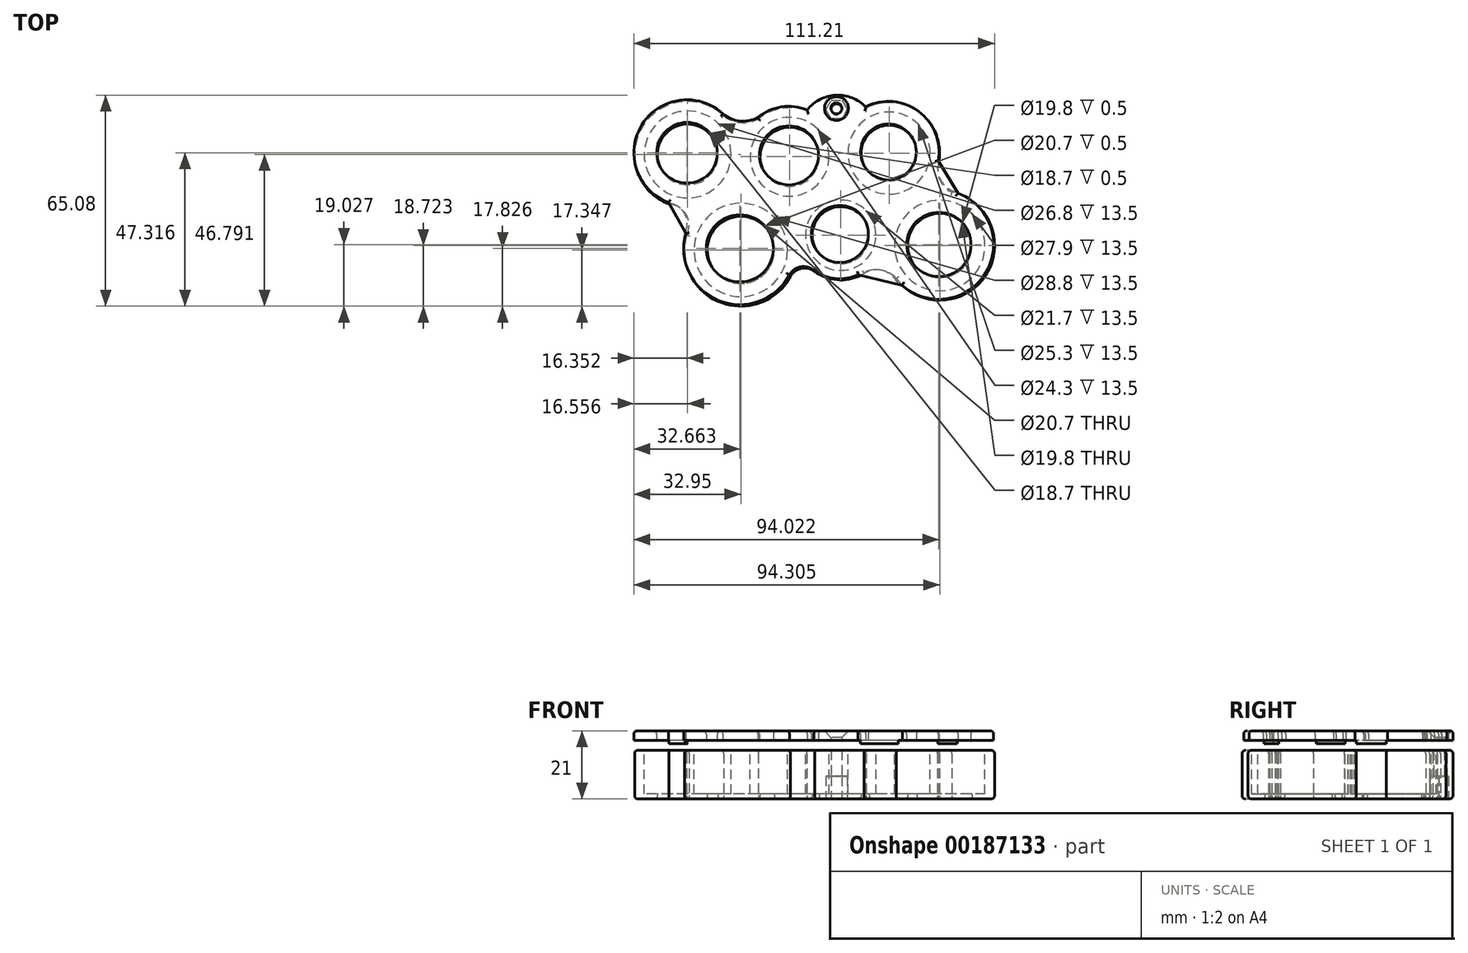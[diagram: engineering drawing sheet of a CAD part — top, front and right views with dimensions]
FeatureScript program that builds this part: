
annotation { "Feature Type Name" : "Feature", "Feature Type Description" : "" }
export const myFeature = defineFeature(function(context is Context, id is Id, definition is map)
    precondition{}
    {
        {
            var Q0;
            Q0=qCreatedBy(makeId("Top.planeOp"),FACE);
            var sketch = newSketch(context, id + "F0", { "sketchPlane" : qUnion([Q0])});
            skArc(sketch, "E0", {"start": v(-18.22, 23.12) * mm, "mid": v(-43.25, 19.71) * mm, "end": v(-35.08, -4.19) * mm});
            skArc(sketch, "E1", {"start": v(7.41, 24.56) * mm, "mid": v(-0.37, 25.32) * mm, "end": v(-7.48, 22.09) * mm});
            skArc(sketch, "E2", {"start": v(48.15, 8.81) * mm, "mid": v(42.1, 24.06) * mm, "end": v(25.77, 25.48) * mm});
            skArc(sketch, "E3", {"start": v(9.86, -25.02) * mm, "mid": v(17.41, -27.58) * mm, "end": v(25.12, -25.54) * mm});
            skArc(sketch, "E4", {"start": v(34.96, -27.17) * mm, "mid": v(62.62, -26.1) * mm, "end": v(52.17, -0.47) * mm});
            skArc(sketch, "E5", {"start": v(-29.65, -13.66) * mm, "mid": v(-19.4, -34.43) * mm, "end": v(2.37, -26.49) * mm});
            skArc(sketch, "E6", {"start": v(-29.65, -13.66) * mm, "mid": v(-29.77, -7.44) * mm, "end": v(-35.08, -4.19) * mm});
            skArc(sketch, "E7", {"start": v(-18.22, 23.12) * mm, "mid": v(-13.01, 20.97) * mm, "end": v(-7.48, 22.09) * mm});
            skArc(sketch, "E8", {"start": v(48.15, 8.81) * mm, "mid": v(48.38, 3.4) * mm, "end": v(52.17, -0.47) * mm});
            skArc(sketch, "E9", {"start": v(34.96, -27.17) * mm, "mid": v(30.34, -24.58) * mm, "end": v(25.12, -25.54) * mm});
            skArc(sketch, "E10", {"start": v(9.86, -25.02) * mm, "mid": v(5.77, -24) * mm, "end": v(2.37, -26.49) * mm});
            skCircle(sketch, "E11", {"center": v(-29.33, 11.12) * mm, "radius": 9.35 * mm});
            skCircle(sketch, "E12", {"center": v(-12.94, -18.32) * mm, "radius": 10.35 * mm});
            skCircle(sketch, "E13", {"center": v(2.1, 10.43) * mm, "radius": 9.1 * mm});
            skCircle(sketch, "E14", {"center": v(17.88, -13.8) * mm, "radius": 8.8 * mm});
            skCircle(sketch, "E15", {"center": v(32.79, 11.55) * mm, "radius": 8.6 * mm});
            skCircle(sketch, "E16", {"center": v(48.42, -16.95) * mm, "radius": 9.9 * mm});
            skPoint(sketch, "E17", {"position": v(17.46, 2.98) * mm});
            skPoint(sketch, "E18.orphan", {"position": v(17.45, 10.99) * mm});
            skPoint(sketch, "E19.orphan", {"position": v(25.33, -1.12) * mm});
            skPoint(sketch, "E20.trimOffspring.end.orphan", {"position": v(10, -1.68) * mm});
            skPoint(sketch, "E21.center.orphan", {"position": v(16.6, 25.02) * mm});
            skArc(sketch, "E22", {"start": v(25.77, 25.48) * mm, "mid": v(16.38, 29.3) * mm, "end": v(7.41, 24.56) * mm});
            skCircle(sketch, "E23", {"center": v(16.6, 25.02) * mm, "radius": 1.7 * mm});
            skSolve(sketch);
        }
        {
            var Q0;
            Q0=makeQuery(id+"F0.imprint","IMPRINT",FACE,{"disambiguationData":[TD([[makeQuery(id+"F0.imprint","IMPRINT",EDGE,{"derivedFrom":sQuery(id+"F0.wireOp",EDGE,"E0")}),1.0]])]});
            extrude(context, id + "F1", {"entities" : qUnion([Q0]), "depth" : 15 * mm});
        }
        {
            var Q0;
            Q0=qCreatedBy(makeId("Top.planeOp"),FACE);
            cPlane(context, id + "F2", {"entities" : qUnion([Q0]), "cplaneType" : CPlaneType.OFFSET, "offset" : 18 * mm, "width" : 150 * mm, "height" : 150 * mm});
        }
        {
            var Q0;
            Q0=makeQuery(id+"F1.opExtrude","CAP_FACE",FACE,{"disambiguationData":[OSD([sQuery(id+"F0.wireOp",EDGE,"E0"),sQuery(id+"F0.wireOp",EDGE,"E1"),sQuery(id+"F0.wireOp",EDGE,"E2"),sQuery(id+"F0.wireOp",EDGE,"E3"),sQuery(id+"F0.wireOp",EDGE,"E4"),sQuery(id+"F0.wireOp",EDGE,"E5"),sQuery(id+"F0.wireOp",EDGE,"E6"),sQuery(id+"F0.wireOp",EDGE,"E7"),sQuery(id+"F0.wireOp",EDGE,"E8"),sQuery(id+"F0.wireOp",EDGE,"E9"),sQuery(id+"F0.wireOp",EDGE,"E10"),sQuery(id+"F0.wireOp",EDGE,"cmuSQvfR-1LlV-bjM8-RssA-lsbDypLqzE8I"),sQuery(id+"F0.wireOp",EDGE,"E21"),sQuery(id+"F0.wireOp",EDGE,"E11"),sQuery(id+"F0.wireOp",EDGE,"E12"),sQuery(id+"F0.wireOp",EDGE,"E13"),sQuery(id+"F0.wireOp",EDGE,"E14"),sQuery(id+"F0.wireOp",EDGE,"E15"),sQuery(id+"F0.wireOp",EDGE,"E16")])],"isStart":false});
            var sketch = newSketch(context, id + "F3", { "sketchPlane" : qUnion([Q0])});
            skCircle(sketch, "E24", {"center": v(-29.33, 11.12) * mm, "radius": 13.4 * mm});
            skCircle(sketch, "E25", {"center": v(-12.94, -18.32) * mm, "radius": 14.4 * mm});
            skCircle(sketch, "E26", {"center": v(17.88, -13.8) * mm, "radius": 10.85 * mm});
            skCircle(sketch, "E27", {"center": v(2.1, 10.43) * mm, "radius": 12.15 * mm});
            skCircle(sketch, "E28", {"center": v(32.79, 11.55) * mm, "radius": 12.65 * mm});
            skCircle(sketch, "E29", {"center": v(48.42, -16.95) * mm, "radius": 13.95 * mm});
            skSolve(sketch);
        }
        {
            var Q0;
            Q0=makeQuery(id+"F3.imprint","IMPRINT",FACE,{"disambiguationData":[TD([[makeQuery(id+"F3.imprint","IMPRINT",EDGE,{"derivedFrom":sQuery(id+"F3.wireOp",EDGE,"E24")}),1.0]])]});
            var Q1;
            Q1=makeQuery(id+"F3.imprint","IMPRINT",FACE,{"disambiguationData":[TD([[makeQuery(id+"F3.imprint","IMPRINT",EDGE,{"derivedFrom":sQuery(id+"F3.wireOp",EDGE,"E27")}),1.0]])]});
            var Q2;
            Q2=makeQuery(id+"F3.imprint","IMPRINT",FACE,{"disambiguationData":[TD([[makeQuery(id+"F3.imprint","IMPRINT",EDGE,{"derivedFrom":sQuery(id+"F3.wireOp",EDGE,"E28")}),1.0]])]});
            var Q3;
            Q3=makeQuery(id+"F3.imprint","IMPRINT",FACE,{"disambiguationData":[TD([[makeQuery(id+"F3.imprint","IMPRINT",EDGE,{"derivedFrom":sQuery(id+"F3.wireOp",EDGE,"E26")}),1.0]])]});
            var Q4;
            Q4=makeQuery(id+"F3.imprint","IMPRINT",FACE,{"disambiguationData":[TD([[makeQuery(id+"F3.imprint","IMPRINT",EDGE,{"derivedFrom":sQuery(id+"F3.wireOp",EDGE,"E25")}),1.0]])]});
            var Q5;
            Q5=makeQuery(id+"F3.imprint","IMPRINT",FACE,{"disambiguationData":[TD([[makeQuery(id+"F3.imprint","IMPRINT",EDGE,{"derivedFrom":sQuery(id+"F3.wireOp",EDGE,"E29")}),1.0]])]});
            extrude(context, id + "F4", {"entities" : qUnion([Q0, Q1, Q2, Q3, Q4, Q5]), "operationType" : NewBodyOperationType.REMOVE, "oppositeDirection" : true, "depth" : 13.5 * mm});
        }
        {
            var Q0;
            Q0=qCreatedBy(makeId("Top.planeOp"),FACE);
            var sketch = newSketch(context, id + "F5", { "sketchPlane" : qUnion([Q0])});
            skPoint(sketch, "E30", {"position": v(16.6, 25.02) * mm});
            skCircle(sketch, "E31.cCircle", {"center": v(16.6, 25.02) * mm, "radius": 2.86 * mm, "construction": true});
            skLineSegment(sketch, "E31.0", {"start": v(18.2, 27.9) * mm, "end": v(19.9, 25.08) * mm});
            skLineSegment(sketch, "E31.1", {"start": v(19.9, 25.08) * mm, "end": v(18.29, 22.2) * mm});
            skLineSegment(sketch, "E31.2", {"start": v(18.29, 22.2) * mm, "end": v(14.99, 22.14) * mm});
            skLineSegment(sketch, "E31.3", {"start": v(14.99, 22.14) * mm, "end": v(13.3, 24.97) * mm});
            skLineSegment(sketch, "E31.4", {"start": v(13.3, 24.97) * mm, "end": v(14.9, 27.85) * mm});
            skLineSegment(sketch, "E31.5", {"start": v(14.9, 27.85) * mm, "end": v(18.2, 27.9) * mm});
            skPoint(sketch, "E31.0.midPoint", {"position": v(19.04, 26.5) * mm});
            skSolve(sketch);
        }
        {
            var Q0;
            Q0=makeQuery(id+"F5.imprint","IMPRINT",FACE,{"disambiguationData":[TD([[makeQuery(id+"F5.imprint","IMPRINT",EDGE,{"derivedFrom":sQuery(id+"F5.wireOp",EDGE,"E31.0")}),-1.0]])]});
            extrude(context, id + "F6", {"entities" : qUnion([Q0]), "operationType" : NewBodyOperationType.REMOVE, "depth" : 7 * mm});
        }
        {
            var Q0;
            Q0=qCreatedBy(id+"F2.planeOp",FACE);
            var sketch = newSketch(context, id + "F7", { "sketchPlane" : qUnion([Q0])});
            skArc(sketch, "E32", {"start": v(-18.43, 23.64) * mm, "mid": v(-43.45, 20.24) * mm, "end": v(-35.28, -3.66) * mm});
            skArc(sketch, "E33", {"start": v(7.53, 24.87) * mm, "mid": v(-0.4, 25.79) * mm, "end": v(-7.7, 22.52) * mm});
            skArc(sketch, "E34", {"start": v(47.94, 9.16) * mm, "mid": v(41.9, 24.4) * mm, "end": v(25.57, 25.83) * mm});
            skArc(sketch, "E35", {"start": v(9.59, -24.63) * mm, "mid": v(17.14, -27.2) * mm, "end": v(24.85, -25.15) * mm});
            skArc(sketch, "E36", {"start": v(34.68, -26.87) * mm, "mid": v(62.34, -25.8) * mm, "end": v(51.88, -0.16) * mm});
            skArc(sketch, "E37", {"start": v(-29.94, -13.18) * mm, "mid": v(-19.68, -33.95) * mm, "end": v(2.08, -26) * mm});
            skArc(sketch, "E38", {"start": v(-29.94, -13.18) * mm, "mid": v(-30, -6.96) * mm, "end": v(-35.28, -3.66) * mm});
            skArc(sketch, "E39", {"start": v(-18.43, 23.64) * mm, "mid": v(-13.23, 21.45) * mm, "end": v(-7.7, 22.52) * mm});
            skArc(sketch, "E40", {"start": v(47.94, 9.16) * mm, "mid": v(48.13, 3.75) * mm, "end": v(51.88, -0.16) * mm});
            skArc(sketch, "E41", {"start": v(34.68, -26.87) * mm, "mid": v(30.07, -24.23) * mm, "end": v(24.85, -25.15) * mm});
            skArc(sketch, "E42", {"start": v(9.59, -24.63) * mm, "mid": v(5.51, -23.57) * mm, "end": v(2.08, -26) * mm});
            skCircle(sketch, "E43", {"center": v(-29.54, 11.65) * mm, "radius": 9.35 * mm});
            skCircle(sketch, "E44", {"center": v(-13.23, -17.84) * mm, "radius": 10.35 * mm});
            skCircle(sketch, "E45", {"center": v(1.9, 10.86) * mm, "radius": 9.1 * mm});
            skCircle(sketch, "E46", {"center": v(17.6, -13.4) * mm, "radius": 8.8 * mm});
            skCircle(sketch, "E47", {"center": v(32.59, 11.9) * mm, "radius": 8.6 * mm});
            skCircle(sketch, "E48", {"center": v(48.13, -16.64) * mm, "radius": 9.9 * mm});
            skLineSegment(sketch, "E49", {"start": v(-29.94, -13.18) * mm, "end": v(-35.28, -3.66) * mm});
            skArc(sketch, "E50", {"start": v(-30.11, -12.87) * mm, "mid": v(-30.27, -7.1) * mm, "end": v(-35.1, -3.97) * mm});
            skArc(sketch, "E51", {"start": v(34.2, -26.79) * mm, "mid": v(30.02, -24.52) * mm, "end": v(25.32, -25.23) * mm});
            skLineSegment(sketch, "E52", {"start": v(54.05, -0.81) * mm, "end": v(47.94, 9.16) * mm});
            skArc(sketch, "E53", {"start": v(48.15, 8.83) * mm, "mid": v(48.9, 2.9) * mm, "end": v(53.84, -0.48) * mm});
            skArc(sketch, "E54", {"start": v(35.61, -28.94) * mm, "mid": v(30.44, -24.61) * mm, "end": v(23.89, -26.18) * mm});
            skLineSegment(sketch, "E55", {"start": v(23.2, -26.02) * mm, "end": v(36.86, -29.23) * mm});
            skPoint(sketch, "E56.center.orphan", {"position": v(16.55, 25.35) * mm});
            skArc(sketch, "E57", {"start": v(7.53, 24.87) * mm, "mid": v(16.65, 23.42) * mm, "end": v(25.57, 25.83) * mm});
            skArc(sketch, "E58", {"start": v(25.57, 25.83) * mm, "mid": v(16.34, 29.4) * mm, "end": v(7.53, 24.87) * mm});
            skCircle(sketch, "E59", {"center": v(16.55, 25.35) * mm, "radius": 1.7 * mm});
            skSolve(sketch);
        }
        {
            var Q0;
            Q0=qSketchRegion(id+"F7",true);
            extrude(context, id + "F8", {"entities" : qUnion([Q0]), "depth" : 3 * mm});
        }
        {
            var Q0;
            {var subQ0=sQuery(id+"F7.wireOp",EDGE,"abFJn2rG-QnjB-3oZD-kfx5-oWbmogYZg01U");Q0=makeQuery(id+"F7.imprint","IMPRINT",FACE,{"disambiguationData":[TD([[makeQuery(id+"F7.imprint","IMPRINT",EDGE,{"derivedFrom":subQ0}),1.0]])]});}
            var Q1;
            {var subQ0=sQuery(id+"F7.wireOp",EDGE,"E50");Q1=makeQuery(id+"F7.imprint","IMPRINT",FACE,{"disambiguationData":[TD([[makeQuery(id+"F7.imprint","IMPRINT",EDGE,{"derivedFrom":subQ0}),1.0]])]});}
            var Q2;
            {var subQ0=sQuery(id+"F7.wireOp",EDGE,"E51");Q2=makeQuery(id+"F7.imprint","IMPRINT",FACE,{"disambiguationData":[TD([[makeQuery(id+"F7.imprint","IMPRINT",EDGE,{"derivedFrom":subQ0}),1.0]])]});}
            var Q3;
            {var subQ0=sQuery(id+"F7.wireOp",EDGE,"E53");Q3=makeQuery(id+"F7.imprint","IMPRINT",FACE,{"disambiguationData":[TD([[makeQuery(id+"F7.imprint","IMPRINT",EDGE,{"derivedFrom":subQ0}),1.0]])]});}
            var Q4;
            {var subQ1=sQuery(id+"F7.wireOp",EDGE,"E54");var subQ3=makeQuery(id+"F7.imprint","IMPRINT",VERTEX,{"disambiguationData":[OD(0.0)],"derivedFrom":subQ1});Q4=makeQuery(id+"F7.imprint","IMPRINT",FACE,{"disambiguationData":[TD([[makeQuery(id+"F7.imprint","IMPRINT",EDGE,{"disambiguationData":[TD([[subQ3,-1.0]])],"derivedFrom":subQ1}),1.0]])]});}
            extrude(context, id + "F9", {"entities" : qUnion([Q0, Q1, Q2, Q3, Q4]), "operationType" : NewBodyOperationType.ADD, "oppositeDirection" : true, "depth" : 1 * mm});
        }
        {
            var Q0;
            Q0=makeQuery(id+"F1.opExtrude","CAP_EDGE",EDGE,{"disambiguationData":[OSD([sQuery(id+"F0.wireOp",EDGE,"E2")])],"isStart":true});
            var Q1;
            Q1=makeQuery(id+"F1.opExtrude","CAP_EDGE",EDGE,{"disambiguationData":[OSD([sQuery(id+"F0.wireOp",EDGE,"cmuSQvfR-1LlV-bjM8-RssA-lsbDypLqzE8I")])],"isStart":true});
            var Q2;
            Q2=makeQuery(id+"F1.opExtrude","CAP_EDGE",EDGE,{"disambiguationData":[OSD([sQuery(id+"F0.wireOp",EDGE,"E1")])],"isStart":true});
            var Q3;
            Q3=makeQuery(id+"F1.opExtrude","CAP_EDGE",EDGE,{"disambiguationData":[OSD([sQuery(id+"F0.wireOp",EDGE,"E7")])],"isStart":true});
            var Q4;
            Q4=makeQuery(id+"F1.opExtrude","CAP_EDGE",EDGE,{"disambiguationData":[OSD([sQuery(id+"F0.wireOp",EDGE,"E0")])],"isStart":true});
            var Q5;
            Q5=makeQuery(id+"F1.opExtrude","CAP_EDGE",EDGE,{"disambiguationData":[OSD([sQuery(id+"F0.wireOp",EDGE,"E6")])],"isStart":true});
            var Q6;
            Q6=makeQuery(id+"F1.opExtrude","CAP_EDGE",EDGE,{"disambiguationData":[OSD([sQuery(id+"F0.wireOp",EDGE,"E5")])],"isStart":true});
            var Q7;
            Q7=makeQuery(id+"F1.opExtrude","CAP_EDGE",EDGE,{"disambiguationData":[OSD([sQuery(id+"F0.wireOp",EDGE,"E10")])],"isStart":true});
            var Q8;
            Q8=makeQuery(id+"F1.opExtrude","CAP_EDGE",EDGE,{"disambiguationData":[OSD([sQuery(id+"F0.wireOp",EDGE,"E3")])],"isStart":true});
            var Q9;
            Q9=makeQuery(id+"F1.opExtrude","CAP_EDGE",EDGE,{"disambiguationData":[OSD([sQuery(id+"F0.wireOp",EDGE,"E9")])],"isStart":true});
            var Q10;
            Q10=makeQuery(id+"F1.opExtrude","CAP_EDGE",EDGE,{"disambiguationData":[OSD([sQuery(id+"F0.wireOp",EDGE,"E4")])],"isStart":true});
            var Q11;
            Q11=makeQuery(id+"F1.opExtrude","CAP_EDGE",EDGE,{"disambiguationData":[OSD([sQuery(id+"F0.wireOp",EDGE,"E8")])],"isStart":true});
            var Q12;
            Q12=makeQuery(id+"F1.opExtrude","CAP_EDGE",EDGE,{"disambiguationData":[OSD([sQuery(id+"F0.wireOp",EDGE,"E2")])],"isStart":false});
            var Q13;
            Q13=makeQuery(id+"F1.opExtrude","CAP_EDGE",EDGE,{"disambiguationData":[OSD([sQuery(id+"F0.wireOp",EDGE,"cmuSQvfR-1LlV-bjM8-RssA-lsbDypLqzE8I")])],"isStart":false});
            var Q14;
            Q14=makeQuery(id+"F1.opExtrude","CAP_EDGE",EDGE,{"disambiguationData":[OSD([sQuery(id+"F0.wireOp",EDGE,"E1")])],"isStart":false});
            var Q15;
            Q15=makeQuery(id+"F1.opExtrude","CAP_EDGE",EDGE,{"disambiguationData":[OSD([sQuery(id+"F0.wireOp",EDGE,"E7")])],"isStart":false});
            var Q16;
            Q16=makeQuery(id+"F1.opExtrude","CAP_EDGE",EDGE,{"disambiguationData":[OSD([sQuery(id+"F0.wireOp",EDGE,"E0")])],"isStart":false});
            var Q17;
            Q17=makeQuery(id+"F1.opExtrude","CAP_EDGE",EDGE,{"disambiguationData":[OSD([sQuery(id+"F0.wireOp",EDGE,"E6")])],"isStart":false});
            var Q18;
            Q18=makeQuery(id+"F1.opExtrude","CAP_EDGE",EDGE,{"disambiguationData":[OSD([sQuery(id+"F0.wireOp",EDGE,"E5")])],"isStart":false});
            var Q19;
            Q19=makeQuery(id+"F1.opExtrude","CAP_EDGE",EDGE,{"disambiguationData":[OSD([sQuery(id+"F0.wireOp",EDGE,"E10")])],"isStart":false});
            var Q20;
            Q20=makeQuery(id+"F1.opExtrude","CAP_EDGE",EDGE,{"disambiguationData":[OSD([sQuery(id+"F0.wireOp",EDGE,"E3")])],"isStart":false});
            var Q21;
            Q21=makeQuery(id+"F1.opExtrude","CAP_EDGE",EDGE,{"disambiguationData":[OSD([sQuery(id+"F0.wireOp",EDGE,"E9")])],"isStart":false});
            var Q22;
            Q22=makeQuery(id+"F1.opExtrude","CAP_EDGE",EDGE,{"disambiguationData":[OSD([sQuery(id+"F0.wireOp",EDGE,"E4")])],"isStart":false});
            var Q23;
            Q23=makeQuery(id+"F1.opExtrude","CAP_EDGE",EDGE,{"disambiguationData":[OSD([sQuery(id+"F0.wireOp",EDGE,"E8")])],"isStart":false});
            var Q24;
            Q24=makeQuery(id+"F1.opExtrude","CAP_EDGE",EDGE,{"disambiguationData":[OSD([sQuery(id+"F0.wireOp",EDGE,"RsfDVoeq-88MK-O4fM-M0ip-vEhRewOvGteJ")])],"isStart":true});
            var Q25;
            Q25=makeQuery(id+"F1.opExtrude","CAP_EDGE",EDGE,{"disambiguationData":[OSD([sQuery(id+"F0.wireOp",EDGE,"RsfDVoeq-88MK-O4fM-M0ip-vEhRewOvGteJ")])],"isStart":false});
            var Q26;
            Q26=makeQuery(id+"F1.opExtrude","CAP_EDGE",EDGE,{"disambiguationData":[OSD([sQuery(id+"F0.wireOp",EDGE,"E22")])],"isStart":false});
            var Q27;
            Q27=makeQuery(id+"F1.opExtrude","CAP_EDGE",EDGE,{"disambiguationData":[OSD([sQuery(id+"F0.wireOp",EDGE,"E22")])],"isStart":true});
            var Q28;
            Q28=makeQuery(id+"F1.opExtrude","CAP_EDGE",EDGE,{"disambiguationData":[OSD([sQuery(id+"F0.wireOp",EDGE,"E13")])],"isStart":true});
            var Q29;
            Q29=makeQuery(id+"F1.opExtrude","CAP_EDGE",EDGE,{"disambiguationData":[OSD([sQuery(id+"F0.wireOp",EDGE,"E15")])],"isStart":true});
            var Q30;
            Q30=makeQuery(id+"F1.opExtrude","CAP_EDGE",EDGE,{"disambiguationData":[OSD([sQuery(id+"F0.wireOp",EDGE,"E16")])],"isStart":true});
            var Q31;
            Q31=makeQuery(id+"F1.opExtrude","CAP_EDGE",EDGE,{"disambiguationData":[OSD([sQuery(id+"F0.wireOp",EDGE,"E14")])],"isStart":true});
            var Q32;
            Q32=makeQuery(id+"F1.opExtrude","CAP_EDGE",EDGE,{"disambiguationData":[OSD([sQuery(id+"F0.wireOp",EDGE,"E12")])],"isStart":true});
            var Q33;
            Q33=makeQuery(id+"F1.opExtrude","CAP_EDGE",EDGE,{"disambiguationData":[OSD([sQuery(id+"F0.wireOp",EDGE,"E11")])],"isStart":true});
            fillet(context, id + "F10", {"entities" : qUnion([Q0, Q1, Q2, Q3, Q4, Q5, Q6, Q7, Q8, Q9, Q10, Q11, Q12, Q13, Q14, Q15, Q16, Q17, Q18, Q19, Q20, Q21, Q22, Q23, Q24, Q25, Q26, Q27, Q28, Q29, Q30, Q31, Q32, Q33]), "radius" : 1 * mm, "tangentPropagation" : true, "allowEdgeOverflow" : false});
        }
        {
            var Q0;
            Q0=makeQuery(id+"F8.opExtrude","CAP_EDGE",EDGE,{"disambiguationData":[OSD([sQuery(id+"F7.wireOp",EDGE,"E45")])],"isStart":false});
            var Q1;
            Q1=makeQuery(id+"F8.opExtrude","CAP_EDGE",EDGE,{"disambiguationData":[OSD([sQuery(id+"F7.wireOp",EDGE,"E43")])],"isStart":false});
            var Q2;
            Q2=makeQuery(id+"F8.opExtrude","CAP_EDGE",EDGE,{"disambiguationData":[OSD([sQuery(id+"F7.wireOp",EDGE,"E44")])],"isStart":false});
            var Q3;
            Q3=makeQuery(id+"F8.opExtrude","CAP_EDGE",EDGE,{"disambiguationData":[OSD([sQuery(id+"F7.wireOp",EDGE,"E46")])],"isStart":false});
            var Q4;
            Q4=makeQuery(id+"F8.opExtrude","CAP_EDGE",EDGE,{"disambiguationData":[OSD([sQuery(id+"F7.wireOp",EDGE,"E47")])],"isStart":false});
            var Q5;
            Q5=makeQuery(id+"F8.opExtrude","CAP_EDGE",EDGE,{"disambiguationData":[OSD([sQuery(id+"F7.wireOp",EDGE,"E48")])],"isStart":false});
            var Q6;
            Q6=makeQuery(id+"F8.opExtrude","CAP_EDGE",EDGE,{"disambiguationData":[OSD([sQuery(id+"F7.wireOp",EDGE,"E52")])],"isStart":false});
            var Q7;
            Q7=makeQuery(id+"F8.opExtrude","CAP_EDGE",EDGE,{"disambiguationData":[OSD([sQuery(id+"F7.wireOp",EDGE,"E36")])],"isStart":false});
            var Q8;
            Q8=makeQuery(id+"F8.opExtrude","CAP_EDGE",EDGE,{"disambiguationData":[OSD([sQuery(id+"F7.wireOp",EDGE,"E55")])],"isStart":false});
            var Q9;
            Q9=makeQuery(id+"F8.opExtrude","CAP_EDGE",EDGE,{"disambiguationData":[OSD([sQuery(id+"F7.wireOp",EDGE,"E35")])],"isStart":false});
            var Q10;
            Q10=makeQuery(id+"F8.opExtrude","CAP_EDGE",EDGE,{"disambiguationData":[OSD([sQuery(id+"F7.wireOp",EDGE,"E42")])],"isStart":false});
            var Q11;
            Q11=makeQuery(id+"F8.opExtrude","CAP_EDGE",EDGE,{"disambiguationData":[OSD([sQuery(id+"F7.wireOp",EDGE,"E37")])],"isStart":false});
            var Q12;
            Q12=makeQuery(id+"F8.opExtrude","CAP_EDGE",EDGE,{"disambiguationData":[OSD([sQuery(id+"F7.wireOp",EDGE,"E49")])],"isStart":false});
            var Q13;
            Q13=makeQuery(id+"F8.opExtrude","CAP_EDGE",EDGE,{"disambiguationData":[OSD([sQuery(id+"F7.wireOp",EDGE,"E32")])],"isStart":false});
            var Q14;
            Q14=makeQuery(id+"F8.opExtrude","CAP_EDGE",EDGE,{"disambiguationData":[OSD([sQuery(id+"F7.wireOp",EDGE,"E39")])],"isStart":false});
            var Q15;
            Q15=makeQuery(id+"F8.opExtrude","CAP_EDGE",EDGE,{"disambiguationData":[OSD([sQuery(id+"F7.wireOp",EDGE,"E33")])],"isStart":false});
            var Q16;
            Q16=makeQuery(id+"F8.opExtrude","CAP_EDGE",EDGE,{"disambiguationData":[OSD([sQuery(id+"F7.wireOp",EDGE,"69c1c0b9-9592-4324-a081-7276ba0f928f")])],"isStart":false});
            var Q17;
            Q17=makeQuery(id+"F8.opExtrude","CAP_EDGE",EDGE,{"disambiguationData":[OSD([sQuery(id+"F7.wireOp",EDGE,"E34")])],"isStart":false});
            var Q18;
            Q18=makeQuery(id+"F8.opExtrude","CAP_EDGE",EDGE,{"disambiguationData":[OSD([sQuery(id+"F7.wireOp",EDGE,"E57")])],"isStart":false});
            var Q19;
            Q19=makeQuery(id+"F8.opExtrude","CAP_EDGE",EDGE,{"disambiguationData":[OSD([sQuery(id+"F7.wireOp",EDGE,"E58")])],"isStart":false});
            fillet(context, id + "F11", {"entities" : qUnion([Q0, Q1, Q2, Q3, Q4, Q5, Q6, Q7, Q8, Q9, Q10, Q11, Q12, Q13, Q14, Q15, Q16, Q17, Q18, Q19]), "radius" : 1 * mm, "tangentPropagation" : true, "allowEdgeOverflow" : false});
        }
        {
            var Q0;
            Q0=makeQuery(id+"F8.opExtrude","CAP_EDGE",EDGE,{"disambiguationData":[OSD([sQuery(id+"F7.wireOp",EDGE,"E59")])],"isStart":false});
            chamfer(context, id + "F12", {"entities" : qUnion([Q0]), "width" : 2 * mm, "tangentPropagation" : true});
        }
    });
